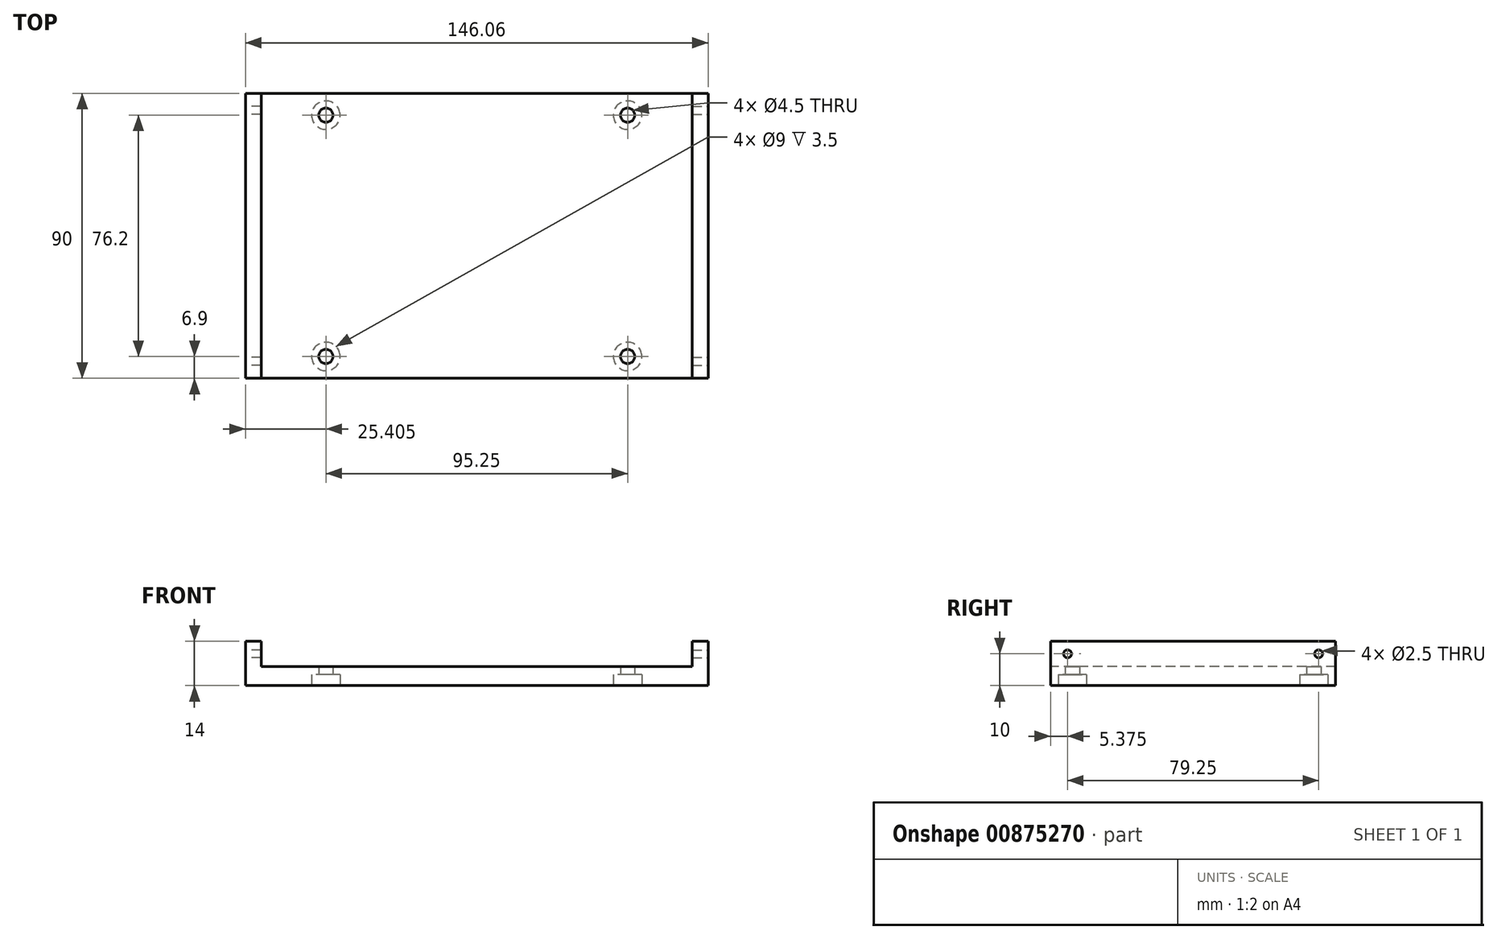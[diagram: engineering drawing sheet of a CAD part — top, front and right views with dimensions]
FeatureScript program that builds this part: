
annotation { "Feature Type Name" : "Feature", "Feature Type Description" : "" }
export const myFeature = defineFeature(function(context is Context, id is Id, definition is map)
    precondition{}
    {
        {
            var Q0;
            Q0=qCreatedBy(makeId("Top.planeOp"),FACE);
            var sketch = newSketch(context, id + "F0", { "sketchPlane" : qUnion([Q0])});
            skLineSegment(sketch, "E0", {"start": v(47.62, 0) * mm, "end": v(-47.62, 0) * mm, "construction": true});
            skLineSegment(sketch, "E1", {"start": v(0, 38.1) * mm, "end": v(0, -38.1) * mm, "construction": true});
            skLineSegment(sketch, "E2", {"start": v(47.62, 38.1) * mm, "end": v(-47.62, 38.1) * mm, "construction": true});
            skLineSegment(sketch, "E3", {"start": v(-47.63, -38.1) * mm, "end": v(47.63, -38.1) * mm, "construction": true});
            skLineSegment(sketch, "E4", {"start": v(47.63, 38.1) * mm, "end": v(47.62, -38.1) * mm, "construction": true});
            skLineSegment(sketch, "E5", {"start": v(-47.62, 38.1) * mm, "end": v(-47.63, -38.1) * mm, "construction": true});
            skPoint(sketch, "E6", {"position": v(0, 38.1) * mm});
            skPoint(sketch, "E7", {"position": v(47.62, 0) * mm});
            skCircle(sketch, "E8", {"center": v(-47.63, -38.1) * mm, "radius": 2.25 * mm});
            skCircle(sketch, "E9", {"center": v(47.63, -38.1) * mm, "radius": 2.25 * mm});
            skCircle(sketch, "E10", {"center": v(47.62, 38.1) * mm, "radius": 2.25 * mm});
            skCircle(sketch, "E11", {"center": v(-47.62, 38.1) * mm, "radius": 2.25 * mm});
            skPoint(sketch, "E12", {"position": v(0, 0) * mm});
            skLineSegment(sketch, "E13.bottom", {"start": v(-73.03, 45) * mm, "end": v(73.03, 45) * mm});
            skLineSegment(sketch, "E13.top", {"start": v(-73.03, -45) * mm, "end": v(73.03, -45) * mm});
            skLineSegment(sketch, "E13.left", {"start": v(-73.03, 45) * mm, "end": v(-73.03, -45) * mm});
            skLineSegment(sketch, "E13.right", {"start": v(73.03, 45) * mm, "end": v(73.03, -45) * mm});
            skCircle(sketch, "E14", {"center": v(-47.62, 38.1) * mm, "radius": 4.5 * mm});
            skCircle(sketch, "E15", {"center": v(-47.63, -38.1) * mm, "radius": 4.5 * mm});
            skCircle(sketch, "E16", {"center": v(47.63, -38.1) * mm, "radius": 4.5 * mm});
            skCircle(sketch, "E17", {"center": v(47.62, 38.1) * mm, "radius": 4.5 * mm});
            skSolve(sketch);
        }
        {
            var Q0;
            Q0=makeQuery(id+"F0.imprint","IMPRINT",FACE,{"disambiguationData":[TD([[makeQuery(id+"F0.imprint","IMPRINT",EDGE,{"derivedFrom":sQuery(id+"F0.wireOp",EDGE,"E13.bottom")}),-1.0]])]});
            var Q1;
            Q1=makeQuery(id+"F0.imprint","IMPRINT",FACE,{"disambiguationData":[TD([[makeQuery(id+"F0.imprint","IMPRINT",EDGE,{"derivedFrom":sQuery(id+"F0.wireOp",EDGE,"E11")}),-1.0]])]});
            var Q2;
            Q2=makeQuery(id+"F0.imprint","IMPRINT",FACE,{"disambiguationData":[TD([[makeQuery(id+"F0.imprint","IMPRINT",EDGE,{"derivedFrom":sQuery(id+"F0.wireOp",EDGE,"E8")}),-1.0]])]});
            var Q3;
            Q3=makeQuery(id+"F0.imprint","IMPRINT",FACE,{"disambiguationData":[TD([[makeQuery(id+"F0.imprint","IMPRINT",EDGE,{"derivedFrom":sQuery(id+"F0.wireOp",EDGE,"E9")}),-1.0]])]});
            var Q4;
            Q4=makeQuery(id+"F0.imprint","IMPRINT",FACE,{"disambiguationData":[TD([[makeQuery(id+"F0.imprint","IMPRINT",EDGE,{"derivedFrom":sQuery(id+"F0.wireOp",EDGE,"E10")}),-1.0]])]});
            extrude(context, id + "F1", {"entities" : qUnion([Q0, Q1, Q2, Q3, Q4]), "depth" : 6 * mm, "offsetDistance" : 25 * mm});
        }
        {
            var Q0;
            Q0=makeQuery(id+"F0.imprint","IMPRINT",FACE,{"disambiguationData":[TD([[makeQuery(id+"F0.imprint","IMPRINT",EDGE,{"derivedFrom":sQuery(id+"F0.wireOp",EDGE,"E11")}),-1.0]])]});
            var Q1;
            Q1=makeQuery(id+"F0.imprint","IMPRINT",FACE,{"disambiguationData":[TD([[makeQuery(id+"F0.imprint","IMPRINT",EDGE,{"derivedFrom":sQuery(id+"F0.wireOp",EDGE,"E8")}),-1.0]])]});
            var Q2;
            Q2=makeQuery(id+"F0.imprint","IMPRINT",FACE,{"disambiguationData":[TD([[makeQuery(id+"F0.imprint","IMPRINT",EDGE,{"derivedFrom":sQuery(id+"F0.wireOp",EDGE,"E9")}),-1.0]])]});
            var Q3;
            Q3=makeQuery(id+"F0.imprint","IMPRINT",FACE,{"disambiguationData":[TD([[makeQuery(id+"F0.imprint","IMPRINT",EDGE,{"derivedFrom":sQuery(id+"F0.wireOp",EDGE,"E10")}),-1.0]])]});
            var Q4;
            Q4=sQuery(id+"F0.wireOp",EDGE,"E14");
            extrude(context, id + "F2", {"entities" : qUnion([Q0, Q1, Q2, Q3]), "operationType" : NewBodyOperationType.REMOVE, "surfaceEntities" : qUnion([Q4]), "depth" : 3.5 * mm, "offsetDistance" : 25 * mm});
        }
        {
            var Q0;
            Q0=makeQuery(id+"F1.opExtrude","SWEPT_FACE",FACE,{"disambiguationData":[OSD([sQuery(id+"F0.wireOp",EDGE,"E13.right")])]});
            var sketch = newSketch(context, id + "F3", { "sketchPlane" : qUnion([Q0])});
            skLineSegment(sketch, "E18.bottom", {"start": v(-45, 14) * mm, "end": v(45, 14) * mm});
            skLineSegment(sketch, "E18.top", {"start": v(-45, 0) * mm, "end": v(45, 0) * mm});
            skLineSegment(sketch, "E18.left", {"start": v(-45, 14) * mm, "end": v(-45, 0) * mm});
            skLineSegment(sketch, "E18.right", {"start": v(45, 14) * mm, "end": v(45, 0) * mm});
            skLineSegment(sketch, "E19", {"start": v(-45, 10) * mm, "end": v(-39.62, 10) * mm, "construction": true});
            skCircle(sketch, "E20", {"center": v(-39.62, 10) * mm, "radius": 1.25 * mm});
            skCircle(sketch, "E21", {"center": v(39.63, 10) * mm, "radius": 1.25 * mm});
            skPoint(sketch, "E22", {"position": v(0, 10) * mm});
            skLineSegment(sketch, "E23", {"start": v(0, 10) * mm, "end": v(39.63, 10) * mm, "construction": true});
            skLineSegment(sketch, "E24", {"start": v(39.63, 10) * mm, "end": v(45, 10) * mm, "construction": true});
            skLineSegment(sketch, "E25", {"start": v(-39.62, 10) * mm, "end": v(0, 10) * mm, "construction": true});
            skSolve(sketch);
        }
        {
            var Q0;
            Q0 = qSketchRegion(id + "F3", true);
            extrude(context, id + "F4", {"entities" : qUnion([Q0]), "operationType" : NewBodyOperationType.ADD, "oppositeDirection" : true, "depth" : 5 * mm, "offsetDistance" : 25 * mm});
        }
        {
            var Q0;
            Q0=makeQuery(id+"F1.opExtrude","SWEPT_FACE",FACE,{"disambiguationData":[OSD([sQuery(id+"F0.wireOp",EDGE,"E13.left")])]});
            var sketch = newSketch(context, id + "F5", { "sketchPlane" : qUnion([Q0])});
            skLineSegment(sketch, "E26.bottom", {"start": v(45, 0) * mm, "end": v(-45, 0) * mm});
            skLineSegment(sketch, "E26.top", {"start": v(45, 14) * mm, "end": v(-45, 14) * mm});
            skLineSegment(sketch, "E26.left", {"start": v(45, 0) * mm, "end": v(45, 14) * mm});
            skLineSegment(sketch, "E26.right", {"start": v(-45, 0) * mm, "end": v(-45, 14) * mm});
            skCircle(sketch, "E27", {"center": v(-39.63, 10) * mm, "radius": 1.25 * mm});
            skCircle(sketch, "E28", {"center": v(39.62, 10) * mm, "radius": 1.25 * mm});
            skSolve(sketch);
        }
        {
            var Q0;
            {var subQ2=sQuery(id+"F5.wireOp",EDGE,"E26.top");Q0=makeQuery(id+"F5.imprint","IMPRINT",FACE,{"disambiguationData":[TD([[makeQuery(id+"F5.imprint","IMPRINT",EDGE,{"derivedFrom":subQ2}),1.0]])]});}
            extrude(context, id + "F6", {"entities" : qUnion([Q0]), "operationType" : NewBodyOperationType.ADD, "oppositeDirection" : true, "depth" : 5 * mm, "offsetDistance" : 25 * mm});
        }
    });
